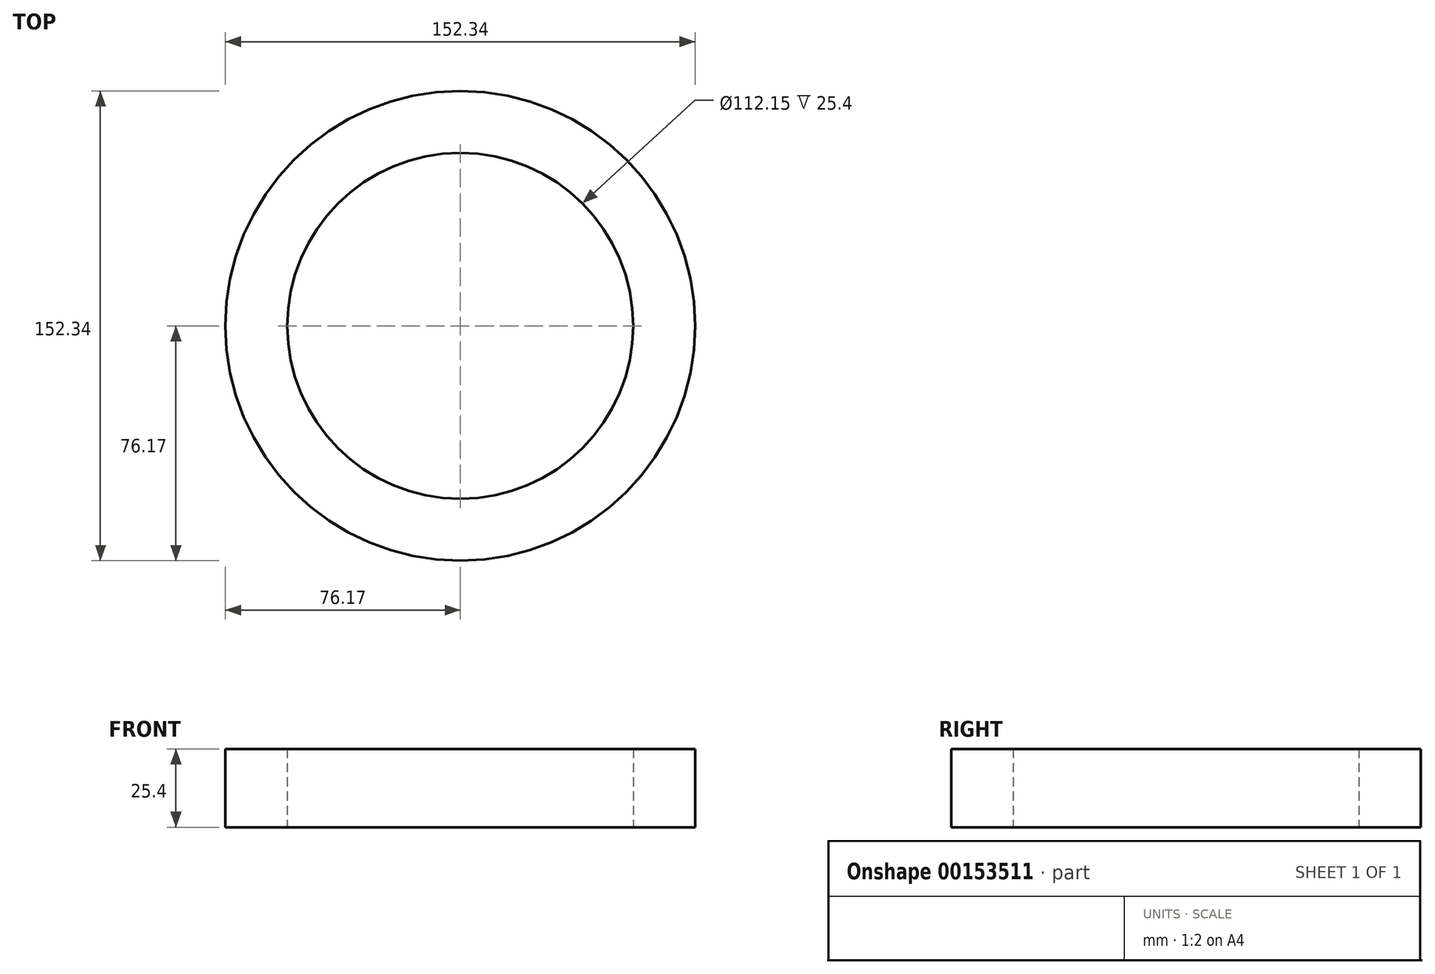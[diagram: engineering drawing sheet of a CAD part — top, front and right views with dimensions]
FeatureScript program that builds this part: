
annotation { "Feature Type Name" : "Feature", "Feature Type Description" : "" }
export const myFeature = defineFeature(function(context is Context, id is Id, definition is map)
    precondition{}
    {
        {
            var Q0;
            Q0=qCreatedBy(makeId("Top.planeOp"),FACE);
            var sketch = newSketch(context, id + "F0", { "sketchPlane" : qUnion([Q0])});
            skCircle(sketch, "E0", {"center": v(0, 0) * mm, "radius": 56.08 * mm});
            skCircle(sketch, "E1", {"center": v(0, 0) * mm, "radius": 76.17 * mm});
            skCircle(sketch, "E2", {"center": v(0, 0) * mm, "radius": 33.83 * mm});
            skSolve(sketch);
        }
        {
            var Q0;
            Q0 = qSketchRegion(id + "F0", true);
            extrude(context, id + "F1", {"entities" : qUnion([Q0]), "depth" : 25.4 * mm});
        }
    });
